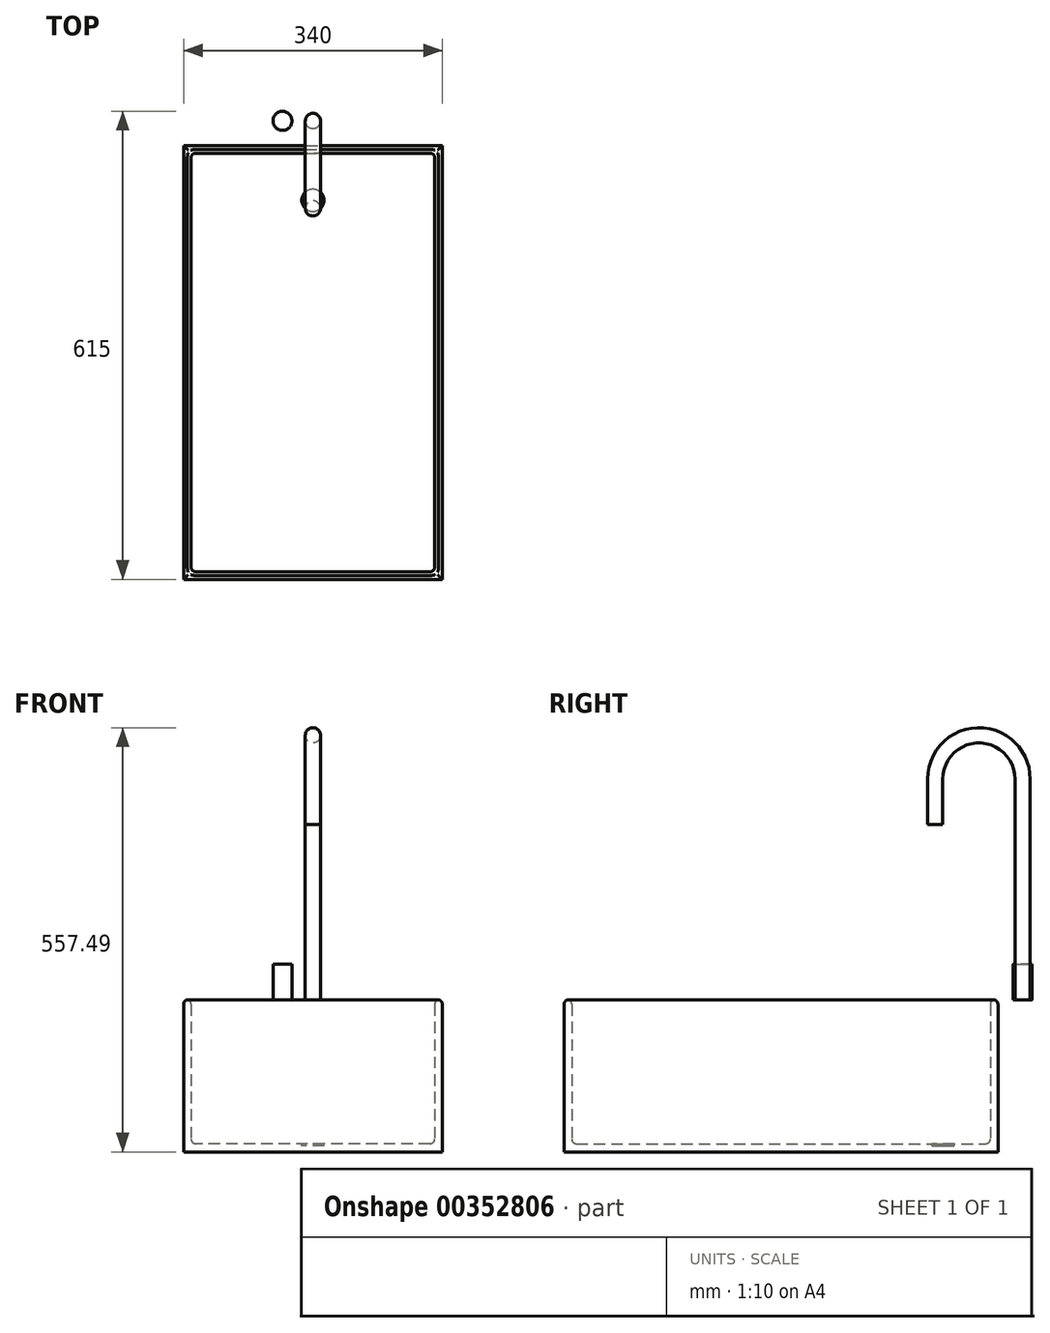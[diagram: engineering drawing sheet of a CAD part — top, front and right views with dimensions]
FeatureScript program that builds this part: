
annotation { "Feature Type Name" : "Feature", "Feature Type Description" : "" }
export const myFeature = defineFeature(function(context is Context, id is Id, definition is map)
    precondition{}
    {
        {
            var Q0;
            Q0=qCreatedBy(makeId("Top.planeOp"),FACE);
            var sketch = newSketch(context, id + "F0", { "sketchPlane" : qUnion([Q0])});
            skLineSegment(sketch, "E0.bottom", {"start": v(-17.58, 539.68) * mm, "end": v(322.42, 539.68) * mm});
            skLineSegment(sketch, "E0.top", {"start": v(-17.58, -30.32) * mm, "end": v(322.42, -30.32) * mm});
            skLineSegment(sketch, "E0.left", {"start": v(-17.58, 539.68) * mm, "end": v(-17.58, -30.32) * mm});
            skLineSegment(sketch, "E0.right", {"start": v(322.42, 539.68) * mm, "end": v(322.42, -30.32) * mm});
            skLineSegment(sketch, "E1.0", {"start": v(-7.58, 529.68) * mm, "end": v(312.42, 529.68) * mm});
            skLineSegment(sketch, "E1.1", {"start": v(-7.58, 529.68) * mm, "end": v(-7.58, -20.32) * mm});
            skLineSegment(sketch, "E1.2", {"start": v(-7.58, -20.32) * mm, "end": v(312.42, -20.32) * mm});
            skLineSegment(sketch, "E1.3", {"start": v(312.42, 529.68) * mm, "end": v(312.42, -20.32) * mm});
            skSolve(sketch);
        }
        {
            var Q0;
            Q0 = qSketchRegion(id + "F0", true);
            extrude(context, id + "F1", {"entities" : qUnion([Q0]), "depth" : 200 * mm});
        }
        {
            var Q0;
            Q0=makeQuery(id+"F1.opExtrude","SWEPT_FACE",FACE,{"disambiguationData":[OSD([sQuery(id+"F0.wireOp",EDGE,"E0.top")])]});
            var sketch = newSketch(context, id + "F2", { "sketchPlane" : qUnion([Q0])});
            skLineSegment(sketch, "E2.bottom", {"start": v(-17.58, 0) * mm, "end": v(322.42, 0) * mm});
            skLineSegment(sketch, "E2.top", {"start": v(-17.58, 10.82) * mm, "end": v(322.42, 10.82) * mm});
            skLineSegment(sketch, "E2.left", {"start": v(-17.58, 0) * mm, "end": v(-17.58, 10.82) * mm});
            skLineSegment(sketch, "E2.right", {"start": v(322.42, 0) * mm, "end": v(322.42, 10.82) * mm});
            skSolve(sketch);
        }
        {
            var Q0;
            Q0 = qSketchRegion(id + "F2", true);
            var Q1;
            Q1=makeQuery(id+"F1.opExtrude","SWEPT_FACE",FACE,{"disambiguationData":[OSD([sQuery(id+"F0.wireOp",EDGE,"E0.bottom")])]});
            extrude(context, id + "F3", {"entities" : qUnion([Q0]), "operationType" : NewBodyOperationType.ADD, "endBound" : BoundingType.UP_TO_SURFACE, "oppositeDirection" : true, "endBoundEntityFace" : qUnion([Q1]), "depth" : 25 * mm});
        }
        {
            var Q0;
            Q0=makeQuery(id+"F1.opExtrude","CAP_FACE",FACE,{"disambiguationData":[OSD([sQuery(id+"F0.wireOp",EDGE,"E0.bottom"),sQuery(id+"F0.wireOp",EDGE,"E0.top"),sQuery(id+"F0.wireOp",EDGE,"E0.left"),sQuery(id+"F0.wireOp",EDGE,"E0.right"),sQuery(id+"F0.wireOp",EDGE,"E1.0"),sQuery(id+"F0.wireOp",EDGE,"E1.1"),sQuery(id+"F0.wireOp",EDGE,"E1.2"),sQuery(id+"F0.wireOp",EDGE,"E1.3")])],"isStart":false});
            var Q1;
            Q1=makeQuery(id+"F3.opExtrude","SWEPT_FACE",FACE,{"disambiguationData":[OSD([sQuery(id+"F2.wireOp",EDGE,"E2.top")])]});
            var Q2;
            Q2=makeQuery(id+"F1.opExtrude","SWEPT_FACE",FACE,{"disambiguationData":[OSD([sQuery(id+"F0.wireOp",EDGE,"E1.0")])]});
            var Q3;
            Q3=makeQuery(id+"F1.opExtrude","SWEPT_EDGE",EDGE,{"disambiguationData":[OSD([sQuery(id+"F0.wireOp",EDGE,"E1.0"),sQuery(id+"F0.wireOp",EDGE,"E1.3")])]});
            var Q4;
            Q4=makeQuery(id+"F1.opExtrude","SWEPT_FACE",FACE,{"disambiguationData":[OSD([sQuery(id+"F0.wireOp",EDGE,"E1.2")])]});
            fillet(context, id + "F4", {"entities" : qUnion([Q0, Q1, Q2, Q3, Q4]), "radius" : 6 * mm, "tangentPropagation" : true, "allowEdgeOverflow" : false});
        }
        {
            var Q0;
            Q0=makeQuery(id+"F3.opExtrude","SWEPT_FACE",FACE,{"disambiguationData":[OSD([sQuery(id+"F2.wireOp",EDGE,"E2.top")])]});
            var sketch = newSketch(context, id + "F5", { "sketchPlane" : qUnion([Q0])});
            skCircle(sketch, "E3", {"center": v(152.42, 467.76) * mm, "radius": 14.59 * mm});
            skPoint(sketch, "E4.orphan", {"position": v(-1.58, 523.68) * mm});
            skPoint(sketch, "E5.end.orphan", {"position": v(306.42, -14.32) * mm});
            skPoint(sketch, "E6.start.orphan", {"position": v(152.42, 254.68) * mm});
            skSolve(sketch);
        }
        {
            var Q0;
            Q0 = qSketchRegion(id + "F5", true);
            extrude(context, id + "F6", {"entities" : qUnion([Q0]), "operationType" : NewBodyOperationType.REMOVE, "oppositeDirection" : true, "depth" : 3 * mm});
        }
        {
            var Q0;
            Q0=qCreatedBy(makeId("Top.planeOp"),FACE);
            cPlane(context, id + "F7", {"entities" : qUnion([Q0]), "cplaneType" : CPlaneType.OFFSET, "offset" : 200 * mm, "width" : 150 * mm, "height" : 150 * mm});
        }
        {
            var Q0;
            Q0=qCreatedBy(id+"F7.planeOp",FACE);
            var sketch = newSketch(context, id + "F8", { "sketchPlane" : qUnion([Q0])});
            skLineSegment(sketch, "E7.0", {"start": v(-17.58, 539.68) * mm, "end": v(322.42, 539.68) * mm});
            skLineSegment(sketch, "E8", {"start": v(152.42, 539.68) * mm, "end": v(152.42, 604.68) * mm});
            skCircle(sketch, "E9", {"center": v(152.42, 572.18) * mm, "radius": 10 * mm});
            skSolve(sketch);
        }
        {
            var Q0;
            Q0=sQuery(id+"F8.wireOp",EDGE,"E8");
            cPlane(context, id + "F9", {"entities" : qUnion([Q0]), "cplaneType" : CPlaneType.LINE_ANGLE, "offset" : 25 * mm, "angle" : 90 * degree, "width" : 150 * mm, "height" : 150 * mm});
        }
        {
            var Q0;
            Q0=qCreatedBy(id+"F9.planeOp",FACE);
            var sketch = newSketch(context, id + "F10", { "sketchPlane" : qUnion([Q0])});
            skLineSegment(sketch, "E10.0", {"start": v(562.18, 200) * mm, "end": v(582.18, 200) * mm});
            skLineSegment(sketch, "E11", {"start": v(572.18, 200) * mm, "end": v(572.18, 430) * mm});
            skLineSegment(sketch, "E12", {"start": v(457.19, 430) * mm, "end": v(457.19, 490) * mm});
            skLineSegment(sketch, "E13", {"start": v(572.18, 430) * mm, "end": v(572.18, 490) * mm});
            skArc(sketch, "E14", {"start": v(572.18, 490) * mm, "mid": v(514.68, 547.5) * mm, "end": v(457.19, 490) * mm});
            skSolve(sketch);
        }
        {
            var Q0;
            Q0 = qSketchRegion(id + "F8", true);
            var Q1;
            Q1=sQuery(id+"F10.wireOp",EDGE,"E11");
            var Q2;
            Q2=sQuery(id+"F10.wireOp",EDGE,"E13");
            var Q3;
            Q3=sQuery(id+"F10.wireOp",EDGE,"E14");
            var Q4;
            Q4=sQuery(id+"F10.wireOp",EDGE,"E12");
            sweep(context, id + "F11", {"profiles" : qUnion([Q0]), "path" : qUnion([Q1, Q2, Q3, Q4])});
        }
        {
            var Q0;
            Q0=qCreatedBy(id+"F7.planeOp",FACE);
            var sketch = newSketch(context, id + "F12", { "sketchPlane" : qUnion([Q0])});
            skCircle(sketch, "E15.0", {"center": v(152.42, 572.18) * mm, "radius": 10 * mm});
            skLineSegment(sketch, "E16", {"start": v(152.42, 572.18) * mm, "end": v(112.42, 572.18) * mm});
            skCircle(sketch, "E17", {"center": v(112.42, 572.18) * mm, "radius": 12.5 * mm});
            skLineSegment(sketch, "E18", {"start": v(152.42, 572.18) * mm, "end": v(152.42, 607.52) * mm});
            skCircle(sketch, "E19.MirrorC", {"center": v(192.42, 572.18) * mm, "radius": 12.5 * mm});
            skSolve(sketch);
        }
        {
            var Q0;
            Q0=makeQuery(id+"F12.imprint","IMPRINT",FACE,{"disambiguationData":[TD([[makeQuery(id+"F12.imprint","IMPRINT",EDGE,{"derivedFrom":sQuery(id+"F12.wireOp",EDGE,"E17")}),1.0]])]});
            var Q1;
            Q1=makeQuery(id+"F12.imprint","IMPRINT",FACE,{"disambiguationData":[TD([[makeQuery(id+"F12.imprint","IMPRINT",EDGE,{"derivedFrom":sQuery(id+"F12.wireOp",EDGE,"E19.MirrorC")}),-1.0]])]});
            extrude(context, id + "F13", {"entities" : qUnion([Q0, Q1]), "depth" : 47 * mm});
        }
    });
